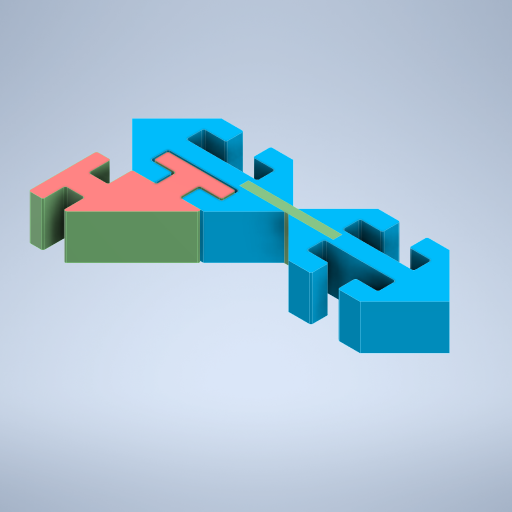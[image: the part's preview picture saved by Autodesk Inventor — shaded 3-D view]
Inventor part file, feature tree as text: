
AUTODESK INVENTOR PART (.ipt)
format: ipt  version: 2023 (Build 270158000, 158)  size: 450,048 bytes
history: native  units: in
note: dims shown in document units (in); Inventor stores cm internally (conversion verified against a paired STEP export)
features: other x3, extrude x3, fillet x3, sketch x1
ambient origin geometry x8: Origin, YZ Plane, XZ Plane, XY Plane, X Axis, Y Axis, Z Axis, Center Point
bodies: Body1 (feature_tree), Body2 (feature_tree), Body3 (feature_tree)
feature tree (10):
  other  "PLA"
  sketch  "Sketch1"  dims[d0=0.4921in d1=0.3937in d2=0.1969in d3=0.1969in d4=0.1969in d5=0.0197in d6=0.0787in d7=0.0787in d8=0.1575in d9=0.0591in d10=0.0984in d11=0.0098in d12=45.0deg d13=0.1969in d14=0.0in d15=0.1969in d16=0.0in d17=0.0079in d18=0.0984in d19=0.1969in d20=0.0in d21=0.0079in d25=0.0079in d26=0.0079in]
  extrude  "Extrusion1"  Depth=0.3937in
  extrude  "Extrusion2"  Depth=0.1969in
  fillet  "Fillet1"  Radius=0.1969in
  extrude  "Extrusion3"  Depth=0.1969in
  fillet  "Fillet2"  Radius=0.0197in
  fillet  "Fillet3"  Radius=0.0787in
  other  "TPU"
  other  "PLA2"
